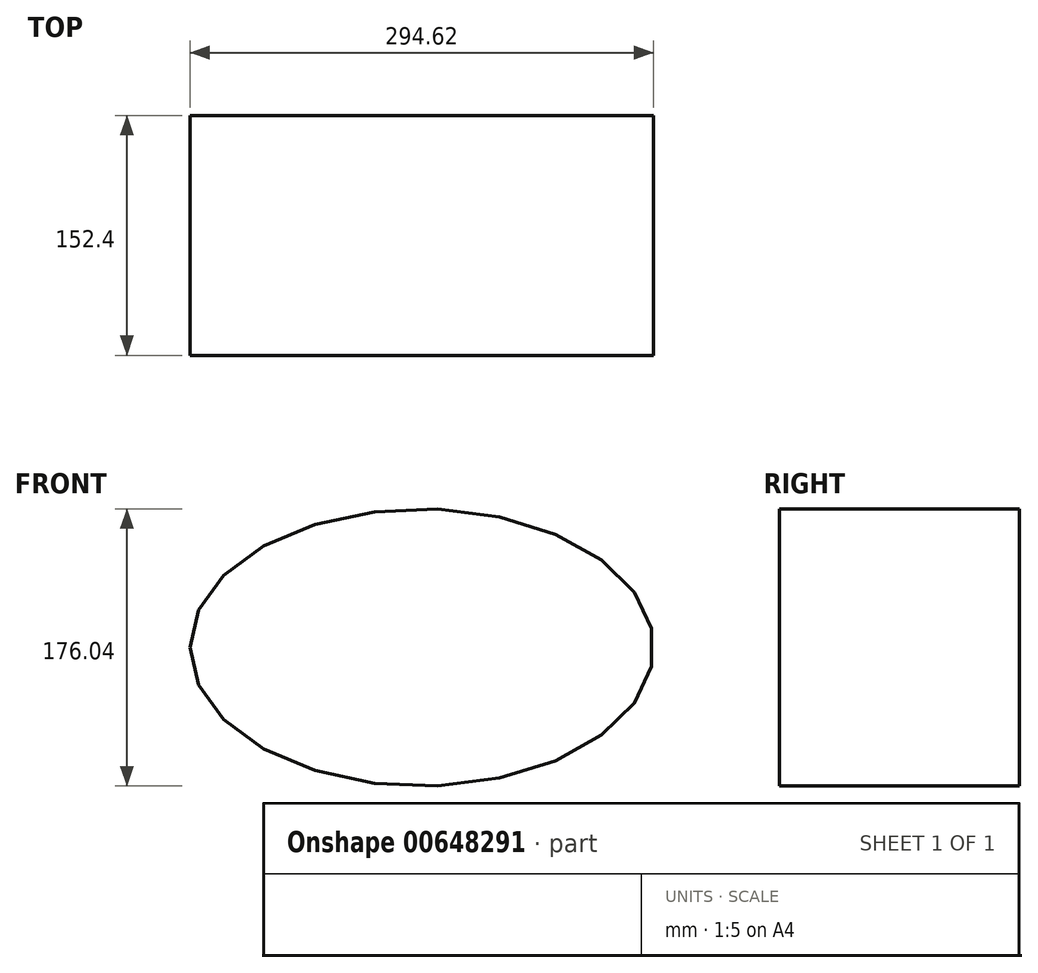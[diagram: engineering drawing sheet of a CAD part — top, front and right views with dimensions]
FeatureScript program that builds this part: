
annotation { "Feature Type Name" : "Feature", "Feature Type Description" : "" }
export const myFeature = defineFeature(function(context is Context, id is Id, definition is map)
    precondition{}
    {
        {
            var Q0;
            Q0=qCreatedBy(makeId("Front.planeOp"),FACE);
            var sketch = newSketch(context, id + "F0", { "sketchPlane" : qUnion([Q0])});
            skEllipse(sketch, "E0", {"center": v(0, 0) * mm, "majorRadius": 147.3 * mm, "minorRadius": 88.02 * mm, "majorAxis": v(-1, 0)});
            skSolve(sketch);
        }
        {
            var Q0;
            Q0=makeQuery(id+"F0.imprint","IMPRINT",FACE,{"disambiguationData":[TD([[makeQuery(id+"F0.imprint","IMPRINT",EDGE,{"derivedFrom":sQuery(id+"F0.wireOp",EDGE,"E0")}),1.0]])]});
            extrude(context, id + "F1", {"entities" : qUnion([Q0]), "depth" : 152.4 * mm, "offsetDistance" : 25.4 * mm});
        }
    });
